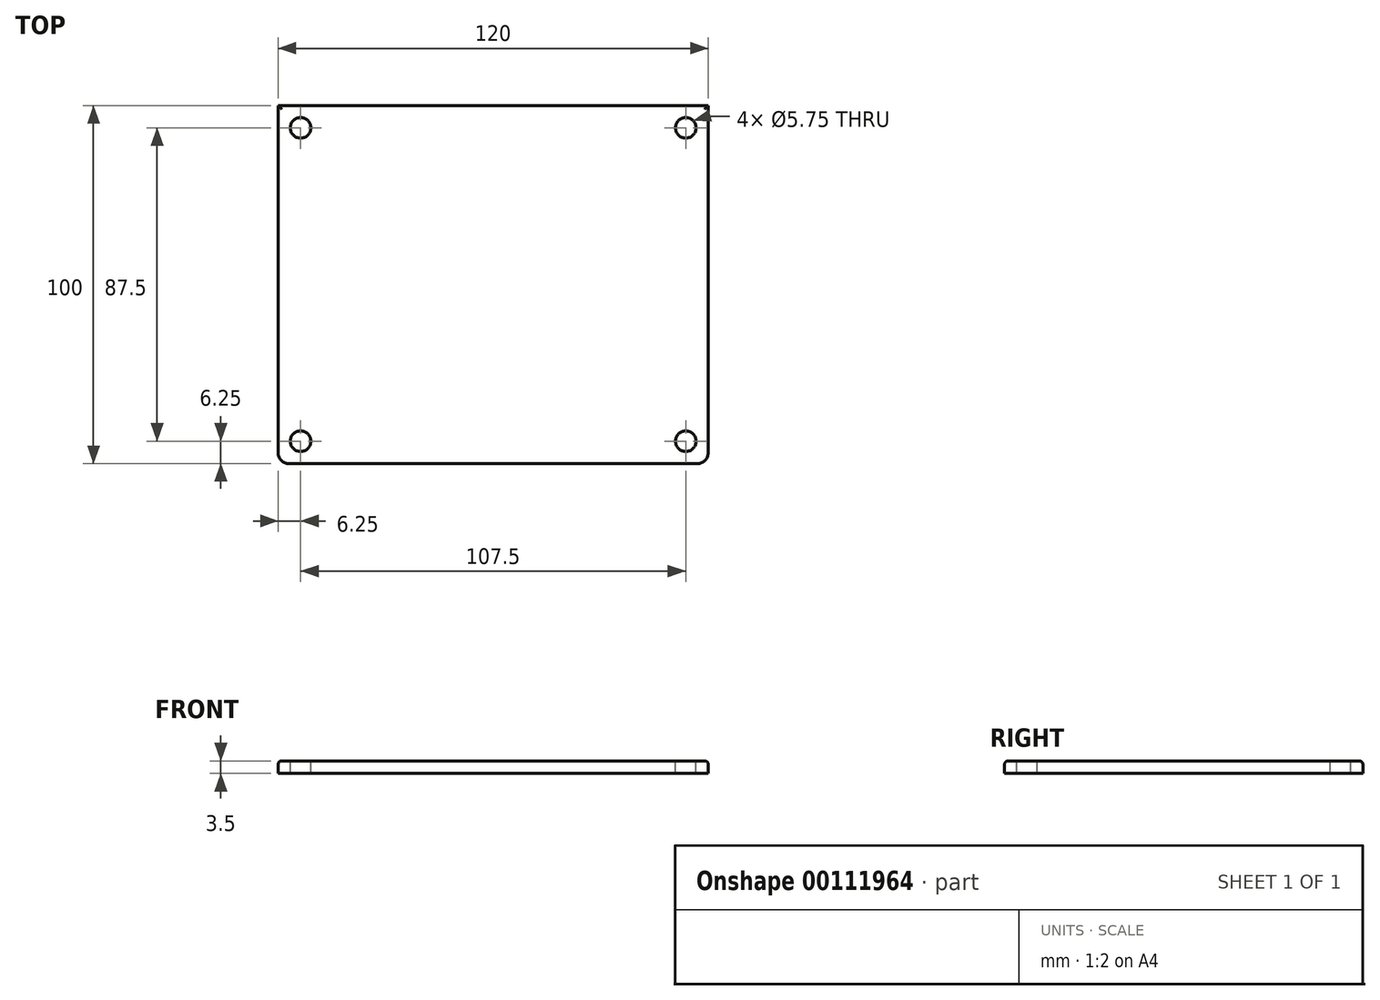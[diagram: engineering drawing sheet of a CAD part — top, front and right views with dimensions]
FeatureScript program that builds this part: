
annotation { "Feature Type Name" : "Feature", "Feature Type Description" : "" }
export const myFeature = defineFeature(function(context is Context, id is Id, definition is map)
    precondition{}
    {
        {
            var Q0;
            Q0=qCreatedBy(makeId("Top.planeOp"),FACE);
            var sketch = newSketch(context, id + "F0", { "sketchPlane" : qUnion([Q0])});
            skLineSegment(sketch, "E0.bottom", {"start": v(57, -50) * mm, "end": v(-57, -50) * mm});
            skLineSegment(sketch, "E0.top", {"start": v(60, 50) * mm, "end": v(-60, 50) * mm});
            skLineSegment(sketch, "E0.left", {"start": v(60, -47) * mm, "end": v(60, 50) * mm});
            skLineSegment(sketch, "E0.right", {"start": v(-60, -47) * mm, "end": v(-60, 50) * mm});
            skPoint(sketch, "E0.middle", {"position": v(0, 0) * mm});
            skPoint(sketch, "E1.visualSharp", {"position": v(60, -50) * mm});
            skArc(sketch, "E1.filletArc", {"start": v(57, -50) * mm, "mid": v(59.12, -49.12) * mm, "end": v(60, -47) * mm});
            skPoint(sketch, "E2.visualSharp", {"position": v(-60, -50) * mm});
            skArc(sketch, "E2.filletArc", {"start": v(-60, -47) * mm, "mid": v(-59.12, -49.12) * mm, "end": v(-57, -50) * mm});
            skSolve(sketch);
        }
        {
            var Q0;
            Q0 = qSketchRegion(id + "F0", true);
            extrude(context, id + "F1", {"entities" : qUnion([Q0]), "depth" : 3.5 * mm});
        }
        {
            var Q0;
            Q0=makeQuery(id+"F1.opExtrude","CAP_FACE",FACE,{"disambiguationData":[OSD([sQuery(id+"F0.wireOp",EDGE,"E0.bottom"),sQuery(id+"F0.wireOp",EDGE,"E0.top"),sQuery(id+"F0.wireOp",EDGE,"E0.left"),sQuery(id+"F0.wireOp",EDGE,"E0.right"),sQuery(id+"F0.wireOp",EDGE,"E1.filletArc"),sQuery(id+"F0.wireOp",EDGE,"E2.filletArc")])],"isStart":false});
            var sketch = newSketch(context, id + "F2", { "sketchPlane" : qUnion([Q0])});
            skPoint(sketch, "E3", {"position": v(0, 0) * mm});
            skLineSegment(sketch, "E4", {"start": v(-60, 43.75) * mm, "end": v(60, 43.75) * mm, "construction": true});
            skLineSegment(sketch, "E5", {"start": v(-60, -43.75) * mm, "end": v(60, -43.75) * mm, "construction": true});
            skLineSegment(sketch, "E6", {"start": v(-53.75, 50) * mm, "end": v(-53.75, -50) * mm, "construction": true});
            skLineSegment(sketch, "E7", {"start": v(53.75, 50) * mm, "end": v(53.75, -50) * mm, "construction": true});
            skPoint(sketch, "E8", {"position": v(-53.75, 43.75) * mm});
            skPoint(sketch, "E9", {"position": v(53.75, 43.75) * mm});
            skPoint(sketch, "E10", {"position": v(53.75, -43.75) * mm});
            skPoint(sketch, "E11", {"position": v(-53.75, -43.75) * mm});
            skCircle(sketch, "E12", {"center": v(-53.75, 43.75) * mm, "radius": 2.88 * mm});
            skCircle(sketch, "E13", {"center": v(53.75, 43.75) * mm, "radius": 2.88 * mm});
            skCircle(sketch, "E14", {"center": v(-53.75, -43.75) * mm, "radius": 2.88 * mm});
            skCircle(sketch, "E15", {"center": v(53.75, -43.75) * mm, "radius": 2.88 * mm});
            skSolve(sketch);
        }
        {
            var Q0;
            Q0 = qSketchRegion(id + "F2", true);
            extrude(context, id + "F3", {"entities" : qUnion([Q0]), "operationType" : NewBodyOperationType.REMOVE, "endBound" : BoundingType.UP_TO_NEXT, "oppositeDirection" : true, "depth" : 25 * mm});
        }
        {
            var Q0;
            Q0=makeQuery(id+"F1.opExtrude","CAP_EDGE",EDGE,{"disambiguationData":[OSD([sQuery(id+"F0.wireOp",EDGE,"E0.bottom")])],"isStart":false});
            var Q1;
            Q1=makeQuery(id+"F1.opExtrude","CAP_EDGE",EDGE,{"disambiguationData":[OSD([sQuery(id+"F0.wireOp",EDGE,"E2.filletArc")])],"isStart":false});
            var Q2;
            Q2=makeQuery(id+"F1.opExtrude","CAP_EDGE",EDGE,{"disambiguationData":[OSD([sQuery(id+"F0.wireOp",EDGE,"E0.right")])],"isStart":false});
            var Q3;
            Q3=makeQuery(id+"F1.opExtrude","CAP_EDGE",EDGE,{"disambiguationData":[OSD([sQuery(id+"F0.wireOp",EDGE,"E0.top")])],"isStart":false});
            var Q4;
            Q4=makeQuery(id+"F1.opExtrude","CAP_EDGE",EDGE,{"disambiguationData":[OSD([sQuery(id+"F0.wireOp",EDGE,"E0.left")])],"isStart":false});
            var Q5;
            Q5=makeQuery(id+"F1.opExtrude","CAP_EDGE",EDGE,{"disambiguationData":[OSD([sQuery(id+"F0.wireOp",EDGE,"E1.filletArc")])],"isStart":false});
            fillet(context, id + "F4", {"entities" : qUnion([Q0, Q1, Q2, Q3, Q4, Q5]), "radius" : 1 * mm, "tangentPropagation" : true, "allowEdgeOverflow" : false});
        }
    });
